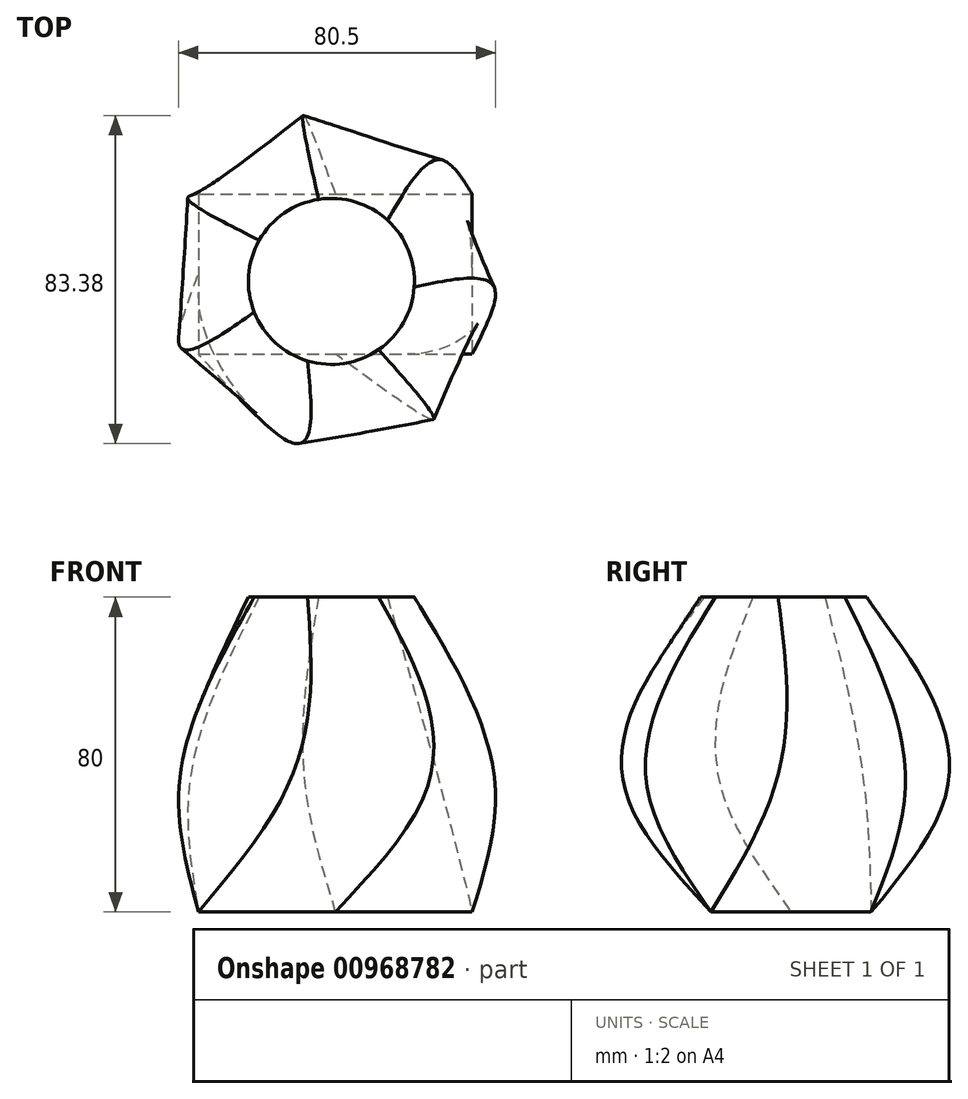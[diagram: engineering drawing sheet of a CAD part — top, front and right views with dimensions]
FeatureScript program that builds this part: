
annotation { "Feature Type Name" : "Feature", "Feature Type Description" : "" }
export const myFeature = defineFeature(function(context is Context, id is Id, definition is map)
    precondition{}
    {
        {
            var Q0;
            Q0=qCreatedBy(makeId("Top.planeOp"),FACE);
            cPlane(context, id + "F0", {"entities" : qUnion([Q0]), "cplaneType" : CPlaneType.OFFSET, "offset" : 50 * mm, "width" : 150 * mm, "height" : 150 * mm});
        }
        {
            var Q0;
            Q0=qCreatedBy(makeId("Top.planeOp"),FACE);
            cPlane(context, id + "F1", {"entities" : qUnion([Q0]), "cplaneType" : CPlaneType.OFFSET, "offset" : 30 * mm, "oppositeDirection" : true, "width" : 150 * mm, "height" : 150 * mm});
        }
        {
            var Q0;
            Q0=qCreatedBy(id+"F0.planeOp",FACE);
            var sketch = newSketch(context, id + "F2", { "sketchPlane" : qUnion([Q0])});
            skCircle(sketch, "E0", {"center": v(0, 0) * mm, "radius": 21.1 * mm});
            skSolve(sketch);
        }
        {
            var Q0;
            Q0=qCreatedBy(makeId("Top.planeOp"),FACE);
            var sketch = newSketch(context, id + "F3", { "sketchPlane" : qUnion([Q0])});
            skCircle(sketch, "E1.cCircle", {"center": v(0, 0) * mm, "radius": 37.63 * mm, "construction": true});
            skLineSegment(sketch, "E1.0", {"start": v(41.67, -2.87) * mm, "end": v(23.74, -34.37) * mm});
            skLineSegment(sketch, "E1.1", {"start": v(23.74, -34.37) * mm, "end": v(-12.07, -39.99) * mm});
            skLineSegment(sketch, "E1.2", {"start": v(-12.07, -39.99) * mm, "end": v(-38.79, -15.5) * mm});
            skLineSegment(sketch, "E1.3", {"start": v(-38.79, -15.5) * mm, "end": v(-36.3, 20.67) * mm});
            skLineSegment(sketch, "E1.4", {"start": v(-36.3, 20.67) * mm, "end": v(-6.47, 41.26) * mm});
            skLineSegment(sketch, "E1.5", {"start": v(-6.47, 41.26) * mm, "end": v(28.23, 30.79) * mm});
            skLineSegment(sketch, "E1.6", {"start": v(28.23, 30.79) * mm, "end": v(41.67, -2.87) * mm});
            skPoint(sketch, "E1.0.midPoint", {"position": v(32.7, -18.62) * mm});
            skSolve(sketch);
        }
        {
            var Q0;
            Q0=qCreatedBy(id+"F1.planeOp",FACE);
            var sketch = newSketch(context, id + "F4", { "sketchPlane" : qUnion([Q0])});
            skLineSegment(sketch, "E2.bottom", {"start": v(-33.78, 22.22) * mm, "end": v(35.77, 22.22) * mm});
            skLineSegment(sketch, "E2.top", {"start": v(-33.78, -18.48) * mm, "end": v(35.77, -18.48) * mm});
            skLineSegment(sketch, "E2.left", {"start": v(-33.78, 22.22) * mm, "end": v(-33.78, -18.48) * mm});
            skLineSegment(sketch, "E2.right", {"start": v(35.77, 22.22) * mm, "end": v(35.77, -18.48) * mm});
            skSolve(sketch);
        }
        {
            var Q0;
            Q0=makeQuery(id+"F2.imprint","IMPRINT",FACE,{"disambiguationData":[TD([[makeQuery(id+"F2.imprint","IMPRINT",EDGE,{"derivedFrom":sQuery(id+"F2.wireOp",EDGE,"E0")}),1.0]])]});
            var Q1;
            Q1=makeQuery(id+"F3.imprint","IMPRINT",FACE,{"disambiguationData":[TD([[makeQuery(id+"F3.imprint","IMPRINT",EDGE,{"derivedFrom":sQuery(id+"F3.wireOp",EDGE,"E1.0")}),-1.0]])]});
            var Q2;
            Q2=makeQuery(id+"F4.imprint","IMPRINT",FACE,{"disambiguationData":[TD([[makeQuery(id+"F4.imprint","IMPRINT",EDGE,{"derivedFrom":sQuery(id+"F4.wireOp",EDGE,"E2.bottom")}),-1.0]])]});
            loft(context, id + "F5", {"sheetProfilesArray" : [{ "sheetProfileEntities" : qUnion([Q0]) }, { "sheetProfileEntities" : qUnion([Q1]) }, { "sheetProfileEntities" : qUnion([Q2]) }]});
        }
    });
